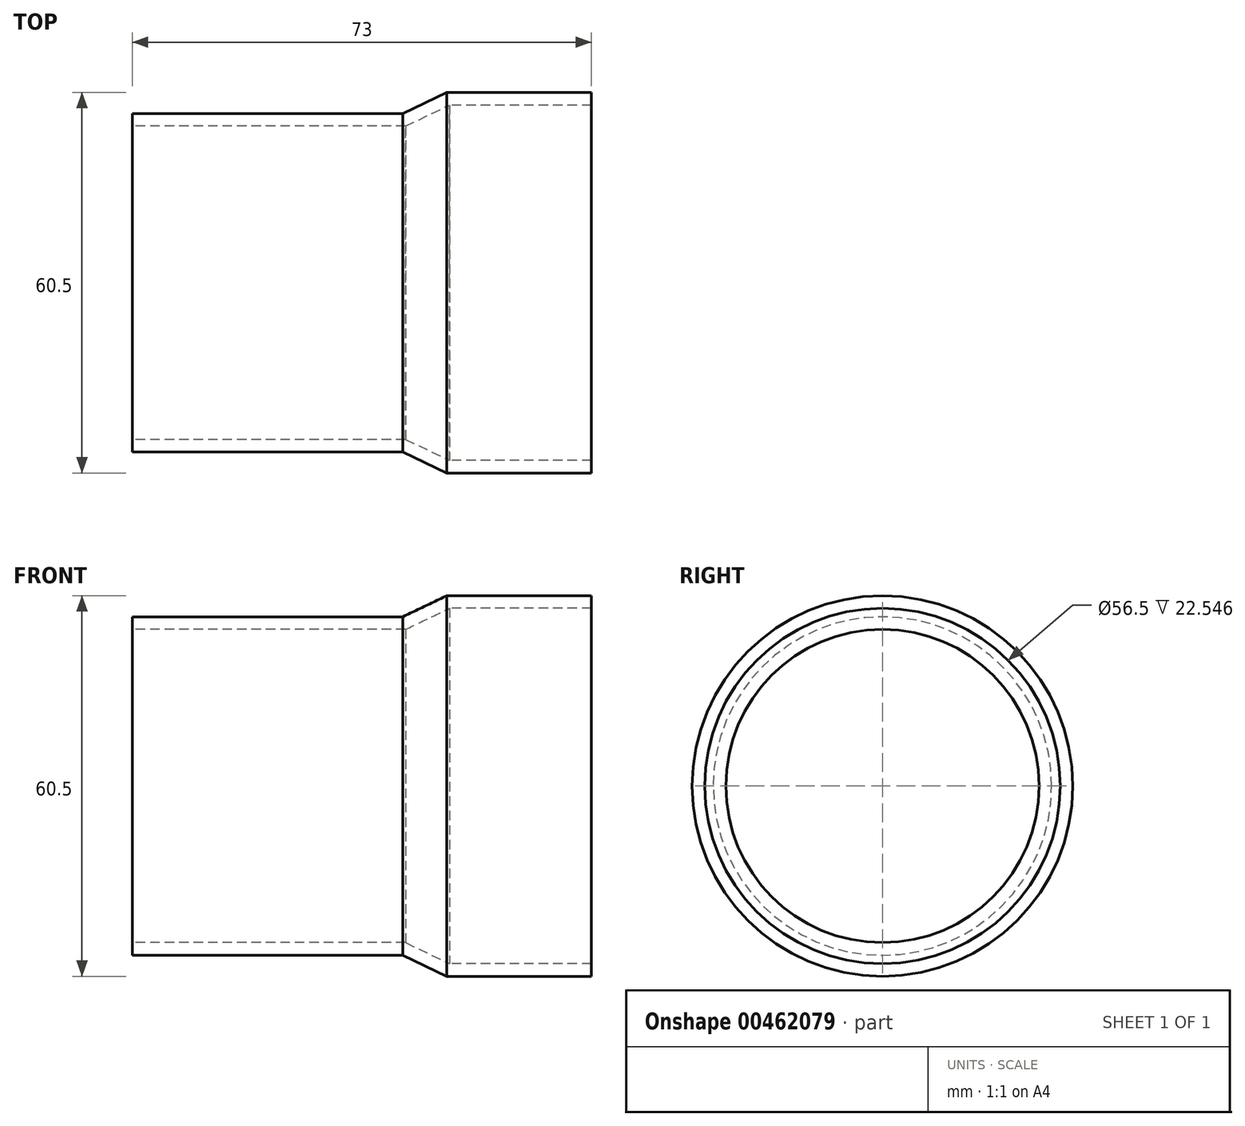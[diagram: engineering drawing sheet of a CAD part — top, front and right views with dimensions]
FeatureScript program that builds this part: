
annotation { "Feature Type Name" : "Feature", "Feature Type Description" : "" }
export const myFeature = defineFeature(function(context is Context, id is Id, definition is map)
    precondition{}
    {
        {
            var Q0;
            Q0=qCreatedBy(makeId("Top.planeOp"),FACE);
            var sketch = newSketch(context, id + "F0", { "sketchPlane" : qUnion([Q0])});
            skLineSegment(sketch, "E0", {"start": v(0, 26.9) * mm, "end": v(43, 26.9) * mm});
            skLineSegment(sketch, "E1", {"start": v(43, 26.9) * mm, "end": v(50, 30.25) * mm});
            skLineSegment(sketch, "E2", {"start": v(50, 30.25) * mm, "end": v(73, 30.25) * mm});
            skLineSegment(sketch, "E3.0", {"start": v(50.45, 28.25) * mm, "end": v(73, 28.25) * mm});
            skLineSegment(sketch, "E3.1", {"start": v(43.45, 24.9) * mm, "end": v(50.45, 28.25) * mm});
            skLineSegment(sketch, "E3.2", {"start": v(0, 24.9) * mm, "end": v(43.45, 24.9) * mm});
            skLineSegment(sketch, "E4", {"start": v(73, 30.25) * mm, "end": v(73, 28.25) * mm});
            skLineSegment(sketch, "E5", {"start": v(0, 26.9) * mm, "end": v(0, 24.9) * mm});
            skLineSegment(sketch, "E6", {"start": v(-66.29, 0) * mm, "end": v(98.01, 0) * mm});
            skSolve(sketch);
        }
        {
            var Q0;
            Q0 = qSketchRegion(id + "F0", true);
            var Q1;
            Q1=sQuery(id+"F0.wireOp",EDGE,"E6");
            revolve(context, id + "F1", {"entities" : qUnion([Q0]), "axis" : qUnion([Q1]), "revolveType" : RevolveType.FULL});
        }
    });
